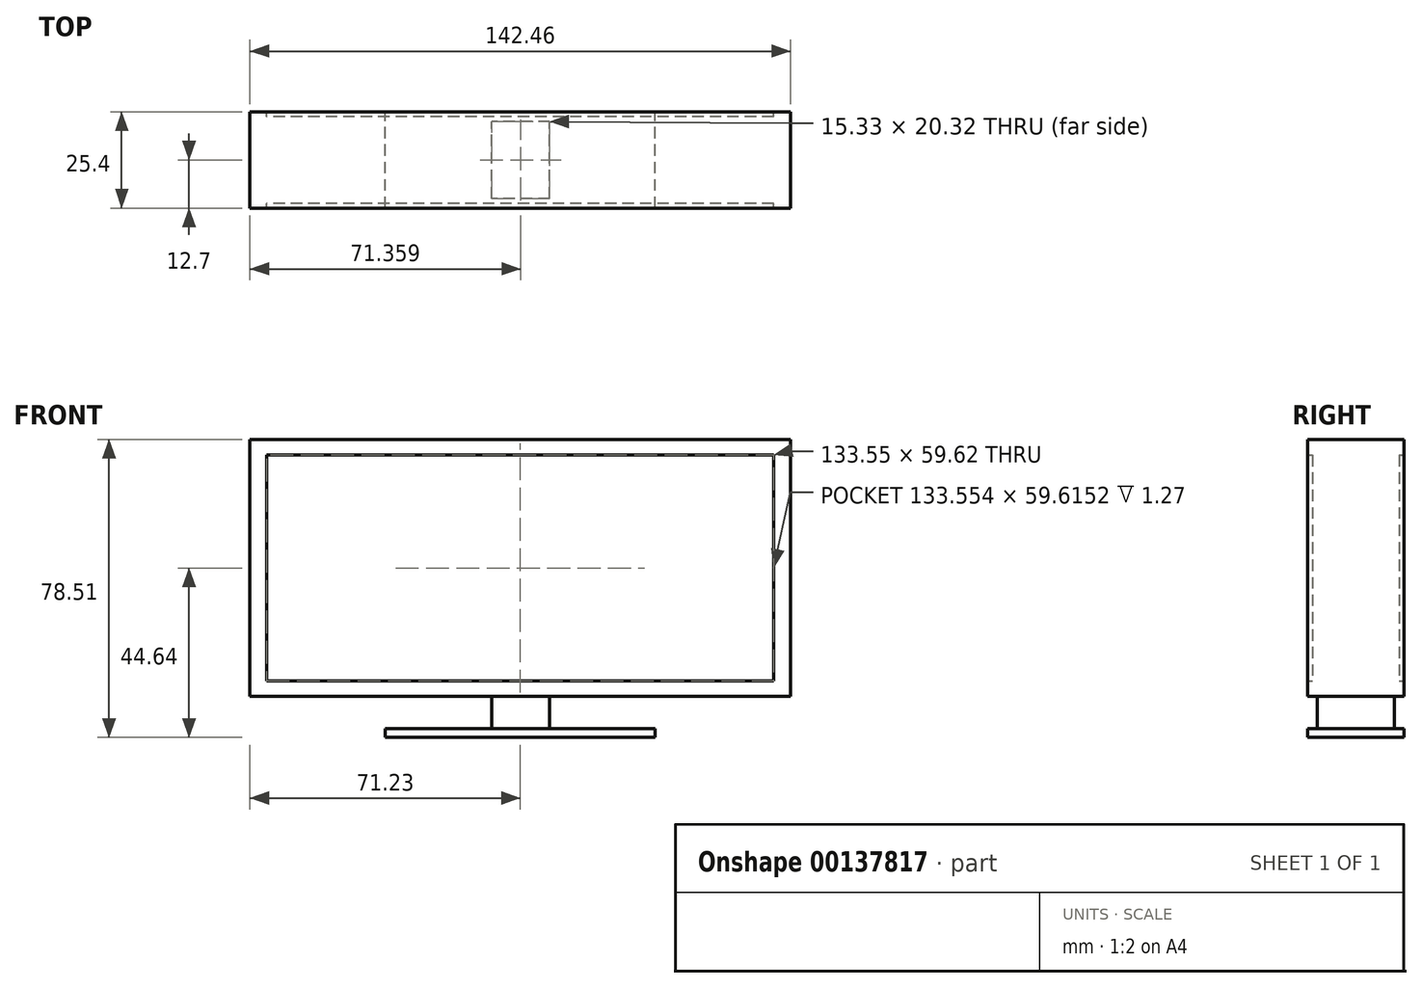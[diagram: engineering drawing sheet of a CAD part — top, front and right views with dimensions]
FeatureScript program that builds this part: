
annotation { "Feature Type Name" : "Feature", "Feature Type Description" : "" }
export const myFeature = defineFeature(function(context is Context, id is Id, definition is map)
    precondition{}
    {
        {
            var Q0;
            Q0=qCreatedBy(makeId("Front.planeOp"),FACE);
            var sketch = newSketch(context, id + "F0", { "sketchPlane" : qUnion([Q0])});
            skLineSegment(sketch, "E0.bottom", {"start": v(71.23, 33.87) * mm, "end": v(-71.23, 33.87) * mm});
            skLineSegment(sketch, "E0.top", {"start": v(71.23, -33.87) * mm, "end": v(-71.23, -33.87) * mm});
            skLineSegment(sketch, "E0.left", {"start": v(71.23, 33.87) * mm, "end": v(71.23, -33.87) * mm});
            skLineSegment(sketch, "E0.right", {"start": v(-71.23, 33.87) * mm, "end": v(-71.23, -33.87) * mm});
            skPoint(sketch, "E0.middle", {"position": v(0, 0) * mm});
            skLineSegment(sketch, "E1", {"start": v(-35.61, -42.33) * mm, "end": v(35.61, -42.33) * mm});
            skLineSegment(sketch, "E2", {"start": v(-7.54, -33.87) * mm, "end": v(-7.54, -42.33) * mm});
            skLineSegment(sketch, "E3", {"start": v(7.8, -33.87) * mm, "end": v(7.8, -42.33) * mm});
            skLineSegment(sketch, "E4", {"start": v(-35.61, -42.33) * mm, "end": v(-35.61, -44.64) * mm});
            skLineSegment(sketch, "E5", {"start": v(-35.61, -44.64) * mm, "end": v(35.61, -44.64) * mm});
            skLineSegment(sketch, "E6", {"start": v(35.61, -44.64) * mm, "end": v(35.61, -42.33) * mm});
            skLineSegment(sketch, "E7.bottom", {"start": v(66.78, 29.8) * mm, "end": v(-66.78, 29.8) * mm});
            skLineSegment(sketch, "E7.top", {"start": v(66.78, -29.8) * mm, "end": v(-66.78, -29.8) * mm});
            skLineSegment(sketch, "E7.left", {"start": v(66.78, 29.8) * mm, "end": v(66.78, -29.8) * mm});
            skLineSegment(sketch, "E7.right", {"start": v(-66.78, 29.8) * mm, "end": v(-66.78, -29.8) * mm});
            skSolve(sketch);
        }
        {
            var Q0;
            Q0=makeQuery(id+"F0.imprint","IMPRINT",FACE,{"disambiguationData":[TD([[makeQuery(id+"F0.imprint","IMPRINT",EDGE,{"derivedFrom":sQuery(id+"F0.wireOp",EDGE,"E0.bottom")}),1.0]])]});
            extrude(context, id + "F1", {"entities" : qUnion([Q0]), "endBound" : BoundingType.SYMMETRIC, "depth" : 25.4 * mm});
        }
        {
            var Q0;
            Q0=makeQuery(id+"F0.imprint","IMPRINT",FACE,{"disambiguationData":[TD([[makeQuery(id+"F0.imprint","IMPRINT",EDGE,{"derivedFrom":sQuery(id+"F0.wireOp",EDGE,"E7.bottom")}),1.0]])]});
            extrude(context, id + "F2", {"entities" : qUnion([Q0]), "operationType" : NewBodyOperationType.ADD, "endBound" : BoundingType.SYMMETRIC, "depth" : 22.86 * mm});
        }
        {
            var Q0;
            {var subQ0=sQuery(id+"F0.wireOp",EDGE,"E2");Q0=makeQuery(id+"F0.imprint","IMPRINT",FACE,{"disambiguationData":[TD([[makeQuery(id+"F0.imprint","IMPRINT",EDGE,{"derivedFrom":subQ0}),1.0]])]});}
            extrude(context, id + "F3", {"entities" : qUnion([Q0]), "operationType" : NewBodyOperationType.ADD, "endBound" : BoundingType.SYMMETRIC, "depth" : 20.32 * mm});
        }
        {
            var Q0;
            {var subQ0=sQuery(id+"F0.wireOp",EDGE,"E4");Q0=makeQuery(id+"F0.imprint","IMPRINT",FACE,{"disambiguationData":[TD([[makeQuery(id+"F0.imprint","IMPRINT",EDGE,{"derivedFrom":subQ0}),1.0]])]});}
            extrude(context, id + "F4", {"entities" : qUnion([Q0]), "operationType" : NewBodyOperationType.ADD, "endBound" : BoundingType.SYMMETRIC, "depth" : 25.4 * mm});
        }
    });
